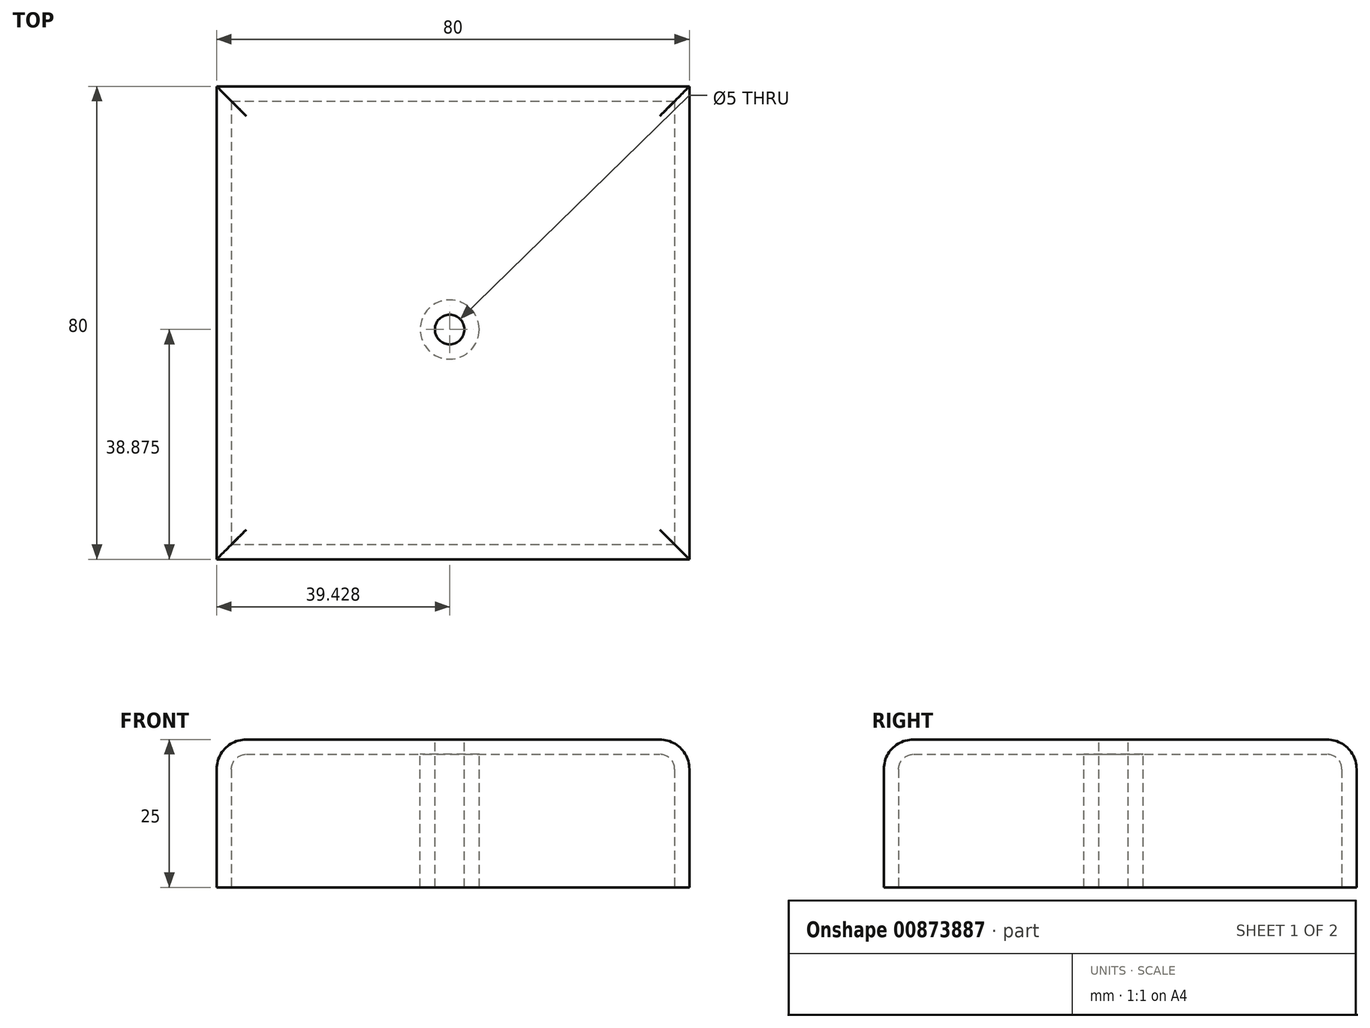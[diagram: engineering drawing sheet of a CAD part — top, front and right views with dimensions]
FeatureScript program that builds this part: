
annotation { "Feature Type Name" : "Feature", "Feature Type Description" : "" }
export const myFeature = defineFeature(function(context is Context, id is Id, definition is map)
    precondition{}
    {
        {
            var Q0;
            Q0=qCreatedBy(makeId("Top.planeOp"),FACE);
            var sketch = newSketch(context, id + "F0", { "sketchPlane" : qUnion([Q0])});
            skLineSegment(sketch, "E0.bottom", {"start": v(-27.25, 53.89) * mm, "end": v(52.75, 53.89) * mm});
            skLineSegment(sketch, "E0.top", {"start": v(-27.25, -26.11) * mm, "end": v(52.75, -26.11) * mm});
            skLineSegment(sketch, "E0.left", {"start": v(-27.25, 53.89) * mm, "end": v(-27.25, -26.11) * mm});
            skLineSegment(sketch, "E0.right", {"start": v(52.75, 53.89) * mm, "end": v(52.75, -26.11) * mm});
            skSolve(sketch);
        }
        {
            var Q0;
            Q0=makeQuery(id+"F0.imprint","IMPRINT",FACE,{"disambiguationData":[TD([[makeQuery(id+"F0.imprint","IMPRINT",EDGE,{"derivedFrom":sQuery(id+"F0.wireOp",EDGE,"E0.bottom")}),-1.0]])]});
            extrude(context, id + "F1", {"entities" : qUnion([Q0]), "depth" : 25 * mm, "offsetDistance" : 25 * mm});
        }
        {
            var Q0;
            Q0=makeQuery(id+"F1.opExtrude","CAP_EDGE",EDGE,{"disambiguationData":[OSD([sQuery(id+"F0.wireOp",EDGE,"E0.right")])],"isStart":false});
            var Q1;
            Q1=makeQuery(id+"F1.opExtrude","CAP_EDGE",EDGE,{"disambiguationData":[OSD([sQuery(id+"F0.wireOp",EDGE,"E0.top")])],"isStart":false});
            var Q2;
            Q2=makeQuery(id+"F1.opExtrude","CAP_EDGE",EDGE,{"disambiguationData":[OSD([sQuery(id+"F0.wireOp",EDGE,"E0.left")])],"isStart":false});
            var Q3;
            Q3=makeQuery(id+"F1.opExtrude","CAP_EDGE",EDGE,{"disambiguationData":[OSD([sQuery(id+"F0.wireOp",EDGE,"E0.bottom")])],"isStart":false});
            fillet(context, id + "F2", {"entities" : qUnion([Q0, Q1, Q2, Q3]), "radius" : 5 * mm, "tangentPropagation" : true, "allowEdgeOverflow" : false});
        }
        {
            var Q0;
            Q0=makeQuery(id+"F1.opExtrude","CAP_FACE",FACE,{"disambiguationData":[OSD([sQuery(id+"F0.wireOp",EDGE,"E0.bottom"),sQuery(id+"F0.wireOp",EDGE,"E0.top"),sQuery(id+"F0.wireOp",EDGE,"E0.left"),sQuery(id+"F0.wireOp",EDGE,"E0.right")])],"isStart":false});
            var sketch = newSketch(context, id + "F3", { "sketchPlane" : qUnion([Q0])});
            skPoint(sketch, "E1", {"position": v(12.18, 12.76) * mm});
            skSolve(sketch);
        }
        {
            var Q0;
            Q0=sQuery(id+"F3.wireOp",VERTEX,"E1");
            var Q1;
            Q1=makeQuery(id+"F1.opExtrude","SWEPT_BODY",BODY,{"disambiguationData":[OSD([sQuery(id+"F0.wireOp",EDGE,"E0.bottom"),sQuery(id+"F0.wireOp",EDGE,"E0.top"),sQuery(id+"F0.wireOp",EDGE,"E0.left"),sQuery(id+"F0.wireOp",EDGE,"E0.right")])]});
            hole(context, id + "F4", {"style" : HoleStyle.SIMPLE, "endStyle" : HoleEndStyle.THROUGH, "holeDiameter" : 5 * mm, "majorDiameter" : 5 * mm, "isTappedThrough" : true, "tappedDepth" : 12 * mm, "tapClearance" : 3, "locations" : qUnion([Q0]), "scope" : qUnion([Q1])});
        }
        {
            var Q0;
            Q0=makeQuery(id+"F1.opExtrude","CAP_FACE",FACE,{"disambiguationData":[OSD([sQuery(id+"F0.wireOp",EDGE,"E0.bottom"),sQuery(id+"F0.wireOp",EDGE,"E0.top"),sQuery(id+"F0.wireOp",EDGE,"E0.left"),sQuery(id+"F0.wireOp",EDGE,"E0.right")])],"isStart":true});
            shell(context, id + "F5", {"entities" : qUnion([Q0]), "thickness" : 2.5 * mm});
        }
    });
